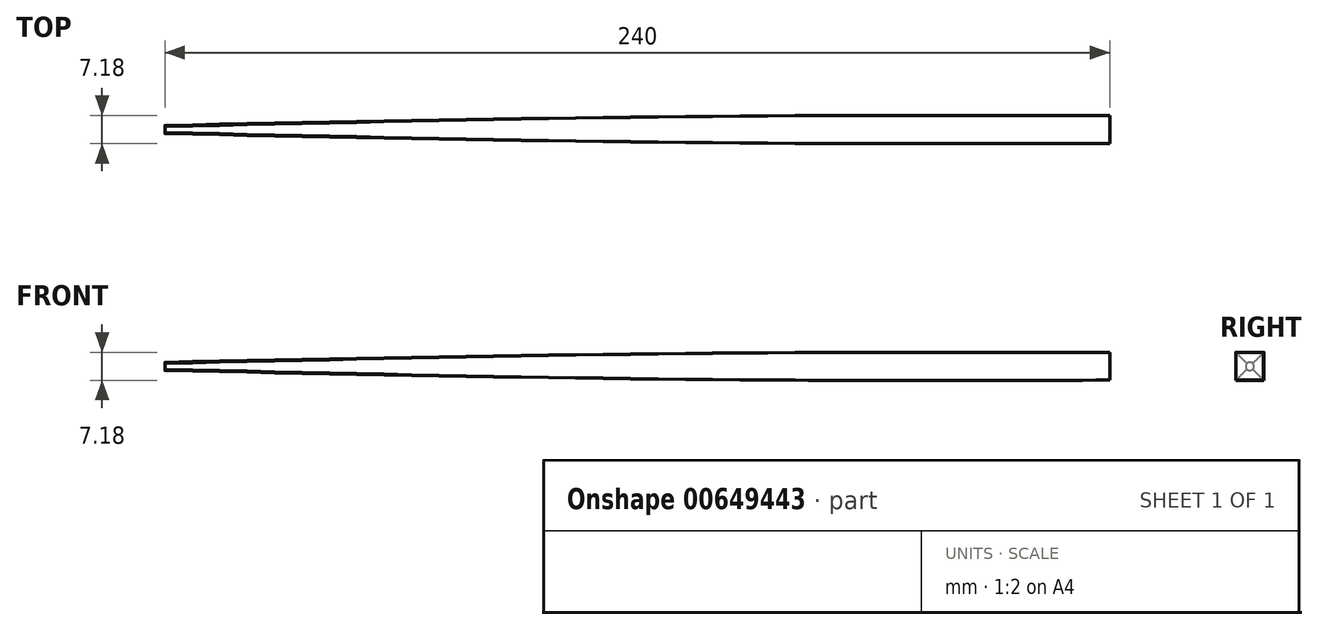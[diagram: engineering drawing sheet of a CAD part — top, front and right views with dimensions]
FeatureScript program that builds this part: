
annotation { "Feature Type Name" : "Feature", "Feature Type Description" : "" }
export const myFeature = defineFeature(function(context is Context, id is Id, definition is map)
    precondition{}
    {
        {
            assignVariable(context, id + "F0", {"name" : "stickLength", "anyValue" : 240});
        }
        {
            assignVariable(context, id + "F1", {"name" : "squareTransition", "anyValue" : (2 / 3) * getVariable(context, 'stickLength')});
        }
        {
            var Q0;
            Q0=qCreatedBy(makeId("Right.planeOp"),FACE);
            var sketch = newSketch(context, id + "F2", { "sketchPlane" : qUnion([Q0])});
            skCircle(sketch, "E0", {"center": v(0, 0) * mm, "radius": 1.05 * mm});
            skSolve(sketch);
        }
        {
            var Q0;
            Q0=qCreatedBy(makeId("Right.planeOp"),FACE);
            cPlane(context, id + "F3", {"entities" : qUnion([Q0]), "cplaneType" : CPlaneType.OFFSET, "offset" : (getVariable(context, 'squareTransition')) * mm, "width" : 150 * mm, "height" : 150 * mm});
        }
        {
            var Q0;
            Q0=qCreatedBy(id+"F3.planeOp",FACE);
            var sketch = newSketch(context, id + "F4", { "sketchPlane" : qUnion([Q0])});
            skLineSegment(sketch, "E1.bottom", {"start": v(3.5, -3.5) * mm, "end": v(-3.5, -3.5) * mm});
            skLineSegment(sketch, "E1.top", {"start": v(3.5, 3.5) * mm, "end": v(-3.5, 3.5) * mm});
            skLineSegment(sketch, "E1.left", {"start": v(3.5, -3.5) * mm, "end": v(3.5, 3.5) * mm});
            skLineSegment(sketch, "E1.right", {"start": v(-3.5, -3.5) * mm, "end": v(-3.5, 3.5) * mm});
            skPoint(sketch, "E1.middle", {"position": v(0, 0) * mm});
            skSolve(sketch);
        }
        {
            var Q0;
            Q0=qCreatedBy(makeId("Right.planeOp"),FACE);
            cPlane(context, id + "F5", {"entities" : qUnion([Q0]), "cplaneType" : CPlaneType.OFFSET, "offset" : (getVariable(context, 'stickLength')) * mm, "width" : 150 * mm, "height" : 150 * mm});
        }
        {
            var Q0;
            Q0=qCreatedBy(id+"F5.planeOp",FACE);
            var sketch = newSketch(context, id + "F6", { "sketchPlane" : qUnion([Q0])});
            skLineSegment(sketch, "E2.bottom", {"start": v(3.5, -3.5) * mm, "end": v(-3.5, -3.5) * mm});
            skLineSegment(sketch, "E2.top", {"start": v(3.5, 3.5) * mm, "end": v(-3.5, 3.5) * mm});
            skLineSegment(sketch, "E2.left", {"start": v(3.5, -3.5) * mm, "end": v(3.5, 3.5) * mm});
            skLineSegment(sketch, "E2.right", {"start": v(-3.5, -3.5) * mm, "end": v(-3.5, 3.5) * mm});
            skPoint(sketch, "E2.middle", {"position": v(0, 0) * mm});
            skSolve(sketch);
        }
        {
            var Q0;
            Q0 = qSketchRegion(id + "F2", true);
            var Q1;
            Q1 = qSketchRegion(id + "F4", true);
            var Q2;
            Q2 = qSketchRegion(id + "F6", true);
            loft(context, id + "F7", {"sheetProfilesArray" : [{ "sheetProfileEntities" : qUnion([Q0]) }, { "sheetProfileEntities" : qUnion([Q1]) }, { "sheetProfileEntities" : qUnion([Q2]) }]});
        }
    });
